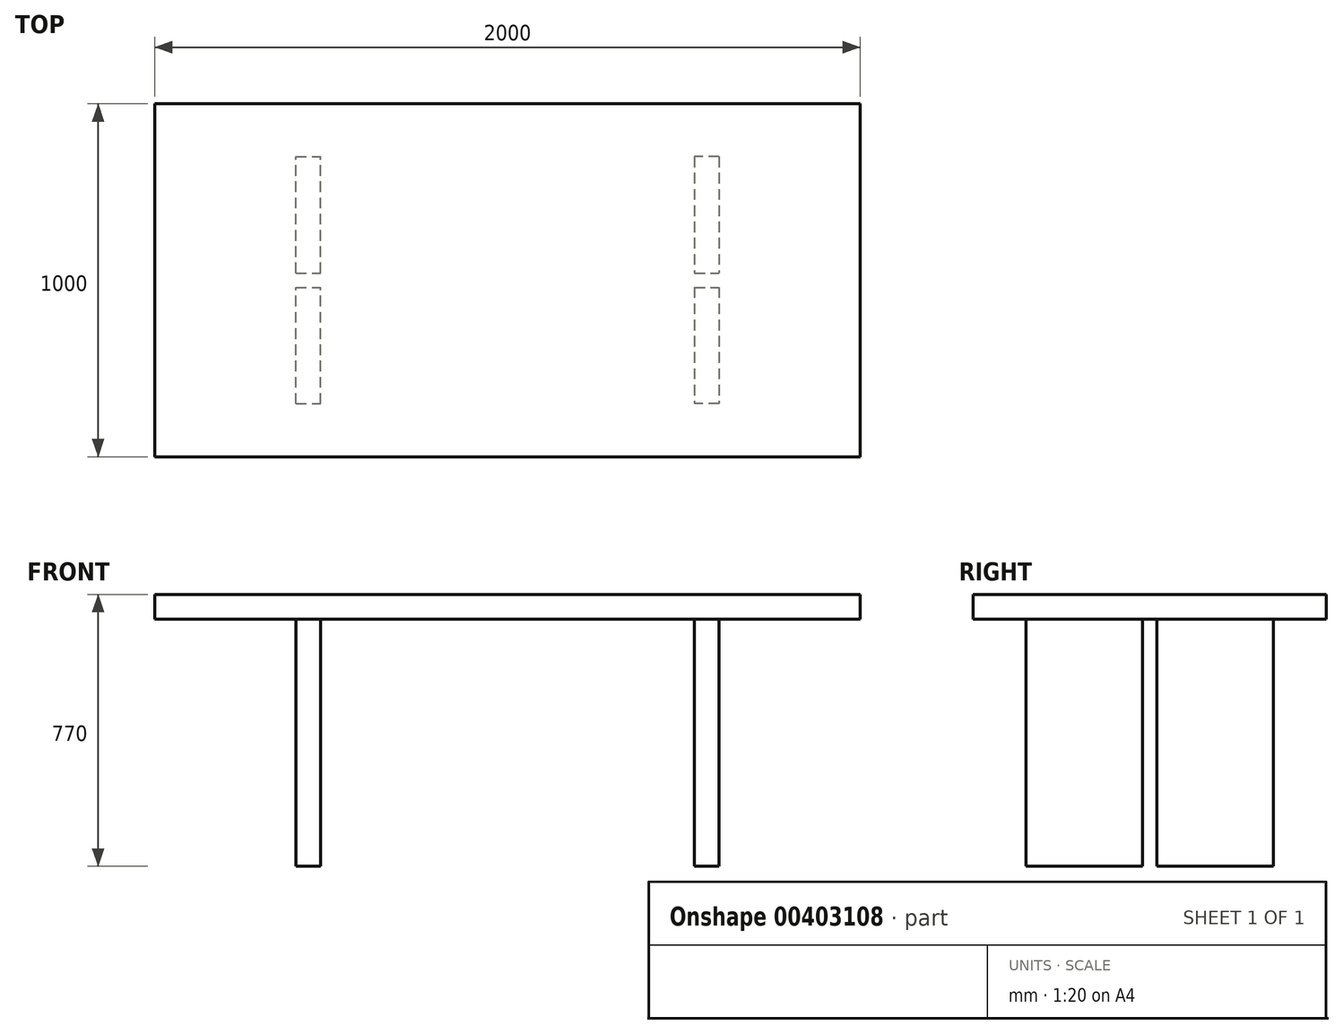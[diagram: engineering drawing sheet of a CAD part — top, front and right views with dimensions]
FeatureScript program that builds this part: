
annotation { "Feature Type Name" : "Feature", "Feature Type Description" : "" }
export const myFeature = defineFeature(function(context is Context, id is Id, definition is map)
    precondition{}
    {
        {
            var Q0;
            Q0=qCreatedBy(makeId("Top.planeOp"),FACE);
            var sketch = newSketch(context, id + "F0", { "sketchPlane" : qUnion([Q0])});
            skLineSegment(sketch, "E0.bottom", {"start": v(0, 0) * mm, "end": v(2000, 0) * mm});
            skLineSegment(sketch, "E0.top", {"start": v(0, 1000) * mm, "end": v(2000, 1000) * mm});
            skLineSegment(sketch, "E0.left", {"start": v(0, 0) * mm, "end": v(0, 1000) * mm});
            skLineSegment(sketch, "E0.right", {"start": v(2000, 0) * mm, "end": v(2000, 1000) * mm});
            skSolve(sketch);
        }
        {
            var Q0;
            Q0 = qSketchRegion(id + "F0", true);
            extrude(context, id + "F1", {"entities" : qUnion([Q0]), "depth" : 70 * mm});
        }
        {
            var Q0;
            Q0=qCreatedBy(makeId("Top.planeOp"),FACE);
            var sketch = newSketch(context, id + "F2", { "sketchPlane" : qUnion([Q0])});
            skLineSegment(sketch, "E1.bottom", {"start": v(400, 150) * mm, "end": v(470, 150) * mm});
            skLineSegment(sketch, "E1.top", {"start": v(400, 850) * mm, "end": v(470, 850) * mm});
            skLineSegment(sketch, "E1.left", {"start": v(400, 150) * mm, "end": v(400, 850) * mm});
            skLineSegment(sketch, "E1.right", {"start": v(470, 150) * mm, "end": v(470, 850) * mm});
            skLineSegment(sketch, "E2.bottom", {"start": v(1600, 850) * mm, "end": v(1530, 850) * mm});
            skLineSegment(sketch, "E2.top", {"start": v(1600, 150) * mm, "end": v(1530, 150) * mm});
            skLineSegment(sketch, "E2.left", {"start": v(1600, 850) * mm, "end": v(1600, 150) * mm});
            skLineSegment(sketch, "E2.right", {"start": v(1530, 850) * mm, "end": v(1530, 150) * mm});
            skLineSegment(sketch, "E3", {"start": v(0, 500) * mm, "end": v(400, 500) * mm, "construction": true});
            skLineSegment(sketch, "E4", {"start": v(2000, 500) * mm, "end": v(1600, 500) * mm, "construction": true});
            skSolve(sketch);
        }
        {
            var Q0;
            Q0 = qSketchRegion(id + "F2", true);
            extrude(context, id + "F3", {"entities" : qUnion([Q0]), "operationType" : NewBodyOperationType.ADD, "oppositeDirection" : true, "depth" : 700 * mm});
        }
        {
            var Q0;
            Q0=makeQuery(id+"F3.opExtrude","SWEPT_FACE",FACE,{"disambiguationData":[OSD([sQuery(id+"F2.wireOp",EDGE,"E2.left")])]});
            var sketch = newSketch(context, id + "F4", { "sketchPlane" : qUnion([Q0])});
            skLineSegment(sketch, "E5.bottom", {"start": v(480, -700) * mm, "end": v(520, -700) * mm});
            skLineSegment(sketch, "E5.top", {"start": v(480, 0) * mm, "end": v(520, 0) * mm});
            skLineSegment(sketch, "E5.left", {"start": v(480, -700) * mm, "end": v(480, 0) * mm});
            skLineSegment(sketch, "E5.right", {"start": v(520, -700) * mm, "end": v(520, 0) * mm});
            skLineSegment(sketch, "E6", {"start": v(500, -700) * mm, "end": v(500, -700) * mm});
            skLineSegment(sketch, "E7", {"start": v(480, -350) * mm, "end": v(150, -350) * mm, "construction": true});
            skSolve(sketch);
        }
        {
            var Q0;
            Q0 = qSketchRegion(id + "F4", true);
            extrude(context, id + "F5", {"entities" : qUnion([Q0]), "operationType" : NewBodyOperationType.REMOVE, "endBound" : BoundingType.THROUGH_ALL, "oppositeDirection" : true, "depth" : 25.4 * mm});
        }
    });
